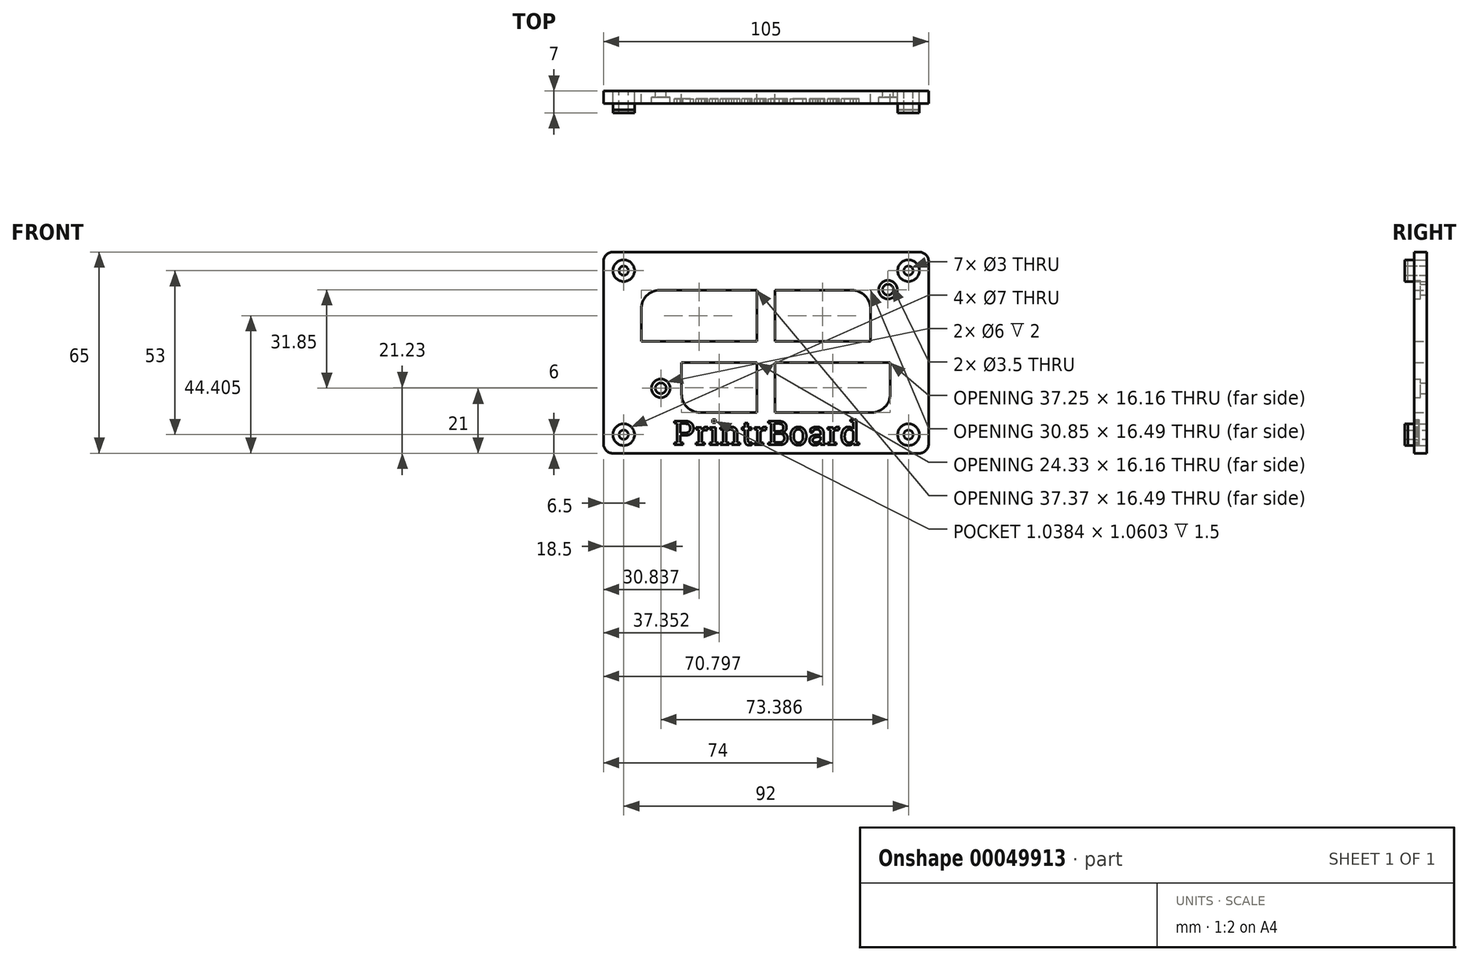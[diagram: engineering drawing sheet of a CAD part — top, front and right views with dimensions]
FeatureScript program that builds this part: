
annotation { "Feature Type Name" : "Feature", "Feature Type Description" : "" }
export const myFeature = defineFeature(function(context is Context, id is Id, definition is map)
    precondition{}
    {
        {
            var Q0;
            Q0=qCreatedBy(makeId("Front.planeOp"),FACE);
            var sketch = newSketch(context, id + "F0", { "sketchPlane" : qUnion([Q0])});
            skLineSegment(sketch, "E0.rect.bottom", {"start": v(46, -26.5) * mm, "end": v(-46, -26.5) * mm, "construction": true});
            skLineSegment(sketch, "E0.rect.top", {"start": v(46, 26.5) * mm, "end": v(-46, 26.5) * mm, "construction": true});
            skLineSegment(sketch, "E0.rect.left", {"start": v(46, -26.5) * mm, "end": v(46, 26.5) * mm, "construction": true});
            skLineSegment(sketch, "E0.rect.right", {"start": v(-46, -26.5) * mm, "end": v(-46, 26.5) * mm, "construction": true});
            skPoint(sketch, "E0.rect.middle", {"position": v(0, 0) * mm});
            skCircle(sketch, "E1", {"center": v(-46, 26.5) * mm, "radius": 3.5 * mm});
            skCircle(sketch, "E2", {"center": v(-46, -26.5) * mm, "radius": 3.5 * mm});
            skCircle(sketch, "E3", {"center": v(46, -26.5) * mm, "radius": 3.5 * mm});
            skCircle(sketch, "E4", {"center": v(46, 26.5) * mm, "radius": 3.5 * mm});
            skCircle(sketch, "E5", {"center": v(46, 26.5) * mm, "radius": 1.5 * mm});
            skCircle(sketch, "E6", {"center": v(46, -26.5) * mm, "radius": 1.5 * mm});
            skCircle(sketch, "E7", {"center": v(-46, -26.5) * mm, "radius": 1.5 * mm});
            skCircle(sketch, "E8", {"center": v(-46, 26.5) * mm, "radius": 1.5 * mm});
            skLineSegment(sketch, "E9.rect.bottom", {"start": v(49.5, -32.5) * mm, "end": v(-49.5, -32.5) * mm});
            skLineSegment(sketch, "E9.rect.top", {"start": v(49.5, 32.5) * mm, "end": v(-49.5, 32.5) * mm});
            skLineSegment(sketch, "E9.rect.left", {"start": v(52.5, -29.5) * mm, "end": v(52.5, 29.5) * mm});
            skLineSegment(sketch, "E9.rect.right", {"start": v(-52.5, -29.5) * mm, "end": v(-52.5, 29.5) * mm});
            skCircle(sketch, "E10", {"center": v(-34, -11.5) * mm, "radius": 3 * mm});
            skCircle(sketch, "E11", {"center": v(39.39, 20.35) * mm, "radius": 3 * mm});
            skCircle(sketch, "E12", {"center": v(-34, -11.5) * mm, "radius": 1.75 * mm});
            skCircle(sketch, "E13", {"center": v(39.39, 20.35) * mm, "radius": 1.75 * mm});
            skLineSegment(sketch, "E14.bottom", {"start": v(-34.35, 20.15) * mm, "end": v(-2.98, 20.15) * mm});
            skLineSegment(sketch, "E14.top", {"start": v(-40.35, 3.66) * mm, "end": v(-2.98, 3.66) * mm});
            skLineSegment(sketch, "E14.left", {"start": v(-40.35, 14.15) * mm, "end": v(-40.35, 3.66) * mm});
            skLineSegment(sketch, "E14.right", {"start": v(-2.98, 20.15) * mm, "end": v(-2.98, 3.66) * mm});
            skLineSegment(sketch, "E15.bottom", {"start": v(-2.98, -3.19) * mm, "end": v(-27.31, -3.19) * mm});
            skLineSegment(sketch, "E15.top", {"start": v(-2.98, -19.35) * mm, "end": v(-21.31, -19.35) * mm});
            skLineSegment(sketch, "E15.left", {"start": v(-2.98, -3.19) * mm, "end": v(-2.98, -19.35) * mm});
            skLineSegment(sketch, "E15.right", {"start": v(-27.31, -3.19) * mm, "end": v(-27.31, -13.35) * mm});
            skLineSegment(sketch, "E16.bottom", {"start": v(2.87, 3.66) * mm, "end": v(33.72, 3.66) * mm});
            skLineSegment(sketch, "E16.top", {"start": v(2.87, 20.15) * mm, "end": v(27.72, 20.15) * mm});
            skLineSegment(sketch, "E16.left", {"start": v(2.87, 3.66) * mm, "end": v(2.87, 20.15) * mm});
            skLineSegment(sketch, "E16.right", {"start": v(33.72, 3.66) * mm, "end": v(33.72, 14.15) * mm});
            skLineSegment(sketch, "E17.bottom", {"start": v(2.87, -3.19) * mm, "end": v(40.13, -3.19) * mm});
            skLineSegment(sketch, "E17.top", {"start": v(2.87, -19.35) * mm, "end": v(34.13, -19.35) * mm});
            skLineSegment(sketch, "E17.left", {"start": v(2.87, -3.19) * mm, "end": v(2.87, -19.35) * mm});
            skLineSegment(sketch, "E17.right", {"start": v(40.13, -3.19) * mm, "end": v(40.13, -13.35) * mm});
            skPoint(sketch, "E18.visualSharp", {"position": v(-40.35, 20.15) * mm});
            skArc(sketch, "E18.filletArc", {"start": v(-34.35, 20.15) * mm, "mid": v(-38.59, 18.4) * mm, "end": v(-40.35, 14.15) * mm});
            skPoint(sketch, "E19.visualSharp", {"position": v(-27.31, -19.35) * mm});
            skArc(sketch, "E19.filletArc", {"start": v(-27.31, -13.35) * mm, "mid": v(-25.56, -17.6) * mm, "end": v(-21.31, -19.35) * mm});
            skPoint(sketch, "E20.visualSharp", {"position": v(40.13, -19.35) * mm});
            skArc(sketch, "E20.filletArc", {"start": v(34.13, -19.35) * mm, "mid": v(38.37, -17.6) * mm, "end": v(40.13, -13.35) * mm});
            skPoint(sketch, "E21.visualSharp", {"position": v(33.72, 20.15) * mm});
            skArc(sketch, "E21.filletArc", {"start": v(33.72, 14.15) * mm, "mid": v(31.96, 18.4) * mm, "end": v(27.72, 20.15) * mm});
            skPoint(sketch, "E22.visualSharp", {"position": v(-52.5, 32.5) * mm});
            skArc(sketch, "E22.filletArc", {"start": v(-49.5, 32.5) * mm, "mid": v(-51.62, 31.62) * mm, "end": v(-52.5, 29.5) * mm});
            skPoint(sketch, "E23.visualSharp", {"position": v(-52.5, -32.5) * mm});
            skArc(sketch, "E23.filletArc", {"start": v(-52.5, -29.5) * mm, "mid": v(-51.62, -31.62) * mm, "end": v(-49.5, -32.5) * mm});
            skPoint(sketch, "E24.visualSharp", {"position": v(52.5, -32.5) * mm});
            skArc(sketch, "E24.filletArc", {"start": v(49.5, -32.5) * mm, "mid": v(51.62, -31.62) * mm, "end": v(52.5, -29.5) * mm});
            skPoint(sketch, "E25.visualSharp", {"position": v(52.5, 32.5) * mm});
            skArc(sketch, "E25.filletArc", {"start": v(52.5, 29.5) * mm, "mid": v(51.62, 31.62) * mm, "end": v(49.5, 32.5) * mm});
            skText(sketch, "E26", { "text": "PrintrBoard", "fontName": "RobotoSlab-Regular.ttf"});
            const initialGuessF0  = {"E26": [-0.02995, -0.0298, 1, 0, 0.00778]};
            skSetInitialGuess(sketch, initialGuessF0);
            skSolve(sketch);
        }
        {
            var Q0;
            Q0=makeQuery(id+"F0.imprint","IMPRINT",FACE,{"disambiguationData":[TD([[makeQuery(id+"F0.imprint","IMPRINT",EDGE,{"derivedFrom":sQuery(id+"F0.wireOp",EDGE,"E2")}),1.0]])]});
            var Q1;
            Q1=makeQuery(id+"F0.imprint","IMPRINT",FACE,{"disambiguationData":[TD([[makeQuery(id+"F0.imprint","IMPRINT",EDGE,{"derivedFrom":sQuery(id+"F0.wireOp",EDGE,"E1")}),1.0]])]});
            var Q2;
            Q2=makeQuery(id+"F0.imprint","IMPRINT",FACE,{"disambiguationData":[TD([[makeQuery(id+"F0.imprint","IMPRINT",EDGE,{"derivedFrom":sQuery(id+"F0.wireOp",EDGE,"E4")}),1.0]])]});
            var Q3;
            Q3=makeQuery(id+"F0.imprint","IMPRINT",FACE,{"disambiguationData":[TD([[makeQuery(id+"F0.imprint","IMPRINT",EDGE,{"derivedFrom":sQuery(id+"F0.wireOp",EDGE,"E3")}),1.0]])]});
            extrude(context, id + "F1", {"entities" : qUnion([Q0, Q1, Q2, Q3]), "depth" : 6 * mm});
        }
        {
            var Q0;
            Q0=makeQuery(id+"F0.imprint","IMPRINT",FACE,{"disambiguationData":[TD([[makeQuery(id+"F0.imprint","IMPRINT",EDGE,{"derivedFrom":sQuery(id+"F0.wireOp",EDGE,"E1")}),-1.0]])]});
            extrude(context, id + "F2", {"entities" : qUnion([Q0]), "depth" : 4 * mm});
        }
        {
            var Q0;
            Q0=makeQuery(id+"F0.imprint","IMPRINT",FACE,{"disambiguationData":[TD([[makeQuery(id+"F0.imprint","IMPRINT",EDGE,{"derivedFrom":sQuery(id+"F0.wireOp",EDGE,"E11")}),1.0]])]});
            var Q1;
            Q1=makeQuery(id+"F0.imprint","IMPRINT",FACE,{"disambiguationData":[TD([[makeQuery(id+"F0.imprint","IMPRINT",EDGE,{"derivedFrom":sQuery(id+"F0.wireOp",EDGE,"E10")}),1.0]])]});
            extrude(context, id + "F3", {"entities" : qUnion([Q0, Q1]), "operationType" : NewBodyOperationType.ADD, "depth" : 1 * mm});
        }
        {
            var Q0;
            Q0=makeQuery(id+"F1.opExtrude","CAP_FACE",FACE,{"disambiguationData":[OSD([sQuery(id+"F0.wireOp",EDGE,"E1"),sQuery(id+"F0.wireOp",EDGE,"E8")])],"isStart":false});
            var Q1;
            Q1=makeQuery(id+"F1.opExtrude","CAP_FACE",FACE,{"disambiguationData":[OSD([sQuery(id+"F0.wireOp",EDGE,"E2"),sQuery(id+"F0.wireOp",EDGE,"E7")])],"isStart":false});
            var Q2;
            Q2=makeQuery(id+"F1.opExtrude","CAP_FACE",FACE,{"disambiguationData":[OSD([sQuery(id+"F0.wireOp",EDGE,"E3"),sQuery(id+"F0.wireOp",EDGE,"E6")])],"isStart":false});
            extrude(context, id + "F4", {"entities" : qUnion([Q0, Q1, Q2]), "depth" : 1 * mm});
        }
        {
            var Q0;
            Q0=makeQuery(id+"F1.opExtrude","CAP_FACE",FACE,{"disambiguationData":[OSD([sQuery(id+"F0.wireOp",EDGE,"E4"),sQuery(id+"F0.wireOp",EDGE,"E5")])],"isStart":false});
            extrude(context, id + "F5", {"entities" : qUnion([Q0]), "operationType" : NewBodyOperationType.ADD, "depth" : 1 * mm});
        }
        {
            var Q0;
            Q0=makeQuery(id+"F3.opExtrude","CAP_FACE",FACE,{"disambiguationData":[OSD([sQuery(id+"F0.wireOp",EDGE,"E11"),sQuery(id+"F0.wireOp",EDGE,"E13")])],"isStart":false});
            var Q1;
            Q1=makeQuery(id+"F3.opExtrude","CAP_FACE",FACE,{"disambiguationData":[OSD([sQuery(id+"F0.wireOp",EDGE,"E10"),sQuery(id+"F0.wireOp",EDGE,"E12")])],"isStart":false});
            extrude(context, id + "F6", {"entities" : qUnion([Q0, Q1]), "operationType" : NewBodyOperationType.ADD, "depth" : 1 * mm});
        }
        {
            var Q0;
            Q0=makeQuery(id+"F0.imprint","IMPRINT",FACE,{"disambiguationData":[TD([[makeQuery(id+"F0.imprint","IMPRINT",EDGE,{"derivedFrom":sQuery(id+"F0.wireOp",EDGE,"E26.sketch_text.stroke-0")}),-1.0]])]});
            var Q1;
            Q1=makeQuery(id+"F0.imprint","IMPRINT",FACE,{"disambiguationData":[TD([[makeQuery(id+"F0.imprint","IMPRINT",EDGE,{"derivedFrom":sQuery(id+"F0.wireOp",EDGE,"E26.sketch_text.stroke-23")}),-1.0]])]});
            var Q2;
            Q2=makeQuery(id+"F0.imprint","IMPRINT",FACE,{"disambiguationData":[TD([[makeQuery(id+"F0.imprint","IMPRINT",EDGE,{"derivedFrom":sQuery(id+"F0.wireOp",EDGE,"E26.sketch_text.stroke-42")}),-1.0]])]});
            var Q3;
            Q3=makeQuery(id+"F0.imprint","IMPRINT",FACE,{"disambiguationData":[TD([[makeQuery(id+"F0.imprint","IMPRINT",EDGE,{"derivedFrom":sQuery(id+"F0.wireOp",EDGE,"E26.sketch_text.stroke-52")}),-1.0]])]});
            var Q4;
            Q4=makeQuery(id+"F0.imprint","IMPRINT",FACE,{"disambiguationData":[TD([[makeQuery(id+"F0.imprint","IMPRINT",EDGE,{"derivedFrom":sQuery(id+"F0.wireOp",EDGE,"E26.sketch_text.stroke-56")}),-1.0]])]});
            var Q5;
            Q5=makeQuery(id+"F0.imprint","IMPRINT",FACE,{"disambiguationData":[TD([[makeQuery(id+"F0.imprint","IMPRINT",EDGE,{"derivedFrom":sQuery(id+"F0.wireOp",EDGE,"E26.sketch_text.stroke-82")}),-1.0]])]});
            var Q6;
            Q6=makeQuery(id+"F0.imprint","IMPRINT",FACE,{"disambiguationData":[TD([[makeQuery(id+"F0.imprint","IMPRINT",EDGE,{"derivedFrom":sQuery(id+"F0.wireOp",EDGE,"E26.sketch_text.stroke-102")}),-1.0]])]});
            var Q7;
            Q7=makeQuery(id+"F0.imprint","IMPRINT",FACE,{"disambiguationData":[TD([[makeQuery(id+"F0.imprint","IMPRINT",EDGE,{"derivedFrom":sQuery(id+"F0.wireOp",EDGE,"E26.sketch_text.stroke-121")}),-1.0]])]});
            var Q8;
            Q8=makeQuery(id+"F0.imprint","IMPRINT",FACE,{"disambiguationData":[TD([[makeQuery(id+"F0.imprint","IMPRINT",EDGE,{"derivedFrom":sQuery(id+"F0.wireOp",EDGE,"E26.sketch_text.stroke-151")}),-1.0]])]});
            var Q9;
            Q9=makeQuery(id+"F0.imprint","IMPRINT",FACE,{"disambiguationData":[TD([[makeQuery(id+"F0.imprint","IMPRINT",EDGE,{"derivedFrom":sQuery(id+"F0.wireOp",EDGE,"E26.sketch_text.stroke-171")}),-1.0]])]});
            var Q10;
            Q10=makeQuery(id+"F0.imprint","IMPRINT",FACE,{"disambiguationData":[TD([[makeQuery(id+"F0.imprint","IMPRINT",EDGE,{"derivedFrom":sQuery(id+"F0.wireOp",EDGE,"E26.sketch_text.stroke-206")}),-1.0]])]});
            var Q11;
            Q11=makeQuery(id+"F0.imprint","IMPRINT",FACE,{"disambiguationData":[TD([[makeQuery(id+"F0.imprint","IMPRINT",EDGE,{"derivedFrom":sQuery(id+"F0.wireOp",EDGE,"E26.sketch_text.stroke-225")}),-1.0]])]});
            extrude(context, id + "F7", {"entities" : qUnion([Q0, Q1, Q2, Q3, Q4, Q5, Q6, Q7, Q8, Q9, Q10, Q11]), "operationType" : NewBodyOperationType.ADD, "depth" : 2.5 * mm});
        }
        {
            var Q0;
            Q0=makeQuery(id+"F0.imprint","IMPRINT",FACE,{"disambiguationData":[TD([[makeQuery(id+"F0.imprint","IMPRINT",EDGE,{"derivedFrom":sQuery(id+"F0.wireOp",EDGE,"E26.sketch_text.stroke-16")}),1.0]])]});
            var Q1;
            Q1=makeQuery(id+"F0.imprint","IMPRINT",FACE,{"disambiguationData":[TD([[makeQuery(id+"F0.imprint","IMPRINT",EDGE,{"derivedFrom":sQuery(id+"F0.wireOp",EDGE,"E26.sketch_text.stroke-144")}),1.0]])]});
            var Q2;
            Q2=makeQuery(id+"F0.imprint","IMPRINT",FACE,{"disambiguationData":[TD([[makeQuery(id+"F0.imprint","IMPRINT",EDGE,{"derivedFrom":sQuery(id+"F0.wireOp",EDGE,"E26.sketch_text.stroke-137")}),1.0]])]});
            var Q3;
            Q3=makeQuery(id+"F0.imprint","IMPRINT",FACE,{"disambiguationData":[TD([[makeQuery(id+"F0.imprint","IMPRINT",EDGE,{"derivedFrom":sQuery(id+"F0.wireOp",EDGE,"E26.sketch_text.stroke-161")}),1.0]])]});
            var Q4;
            Q4=makeQuery(id+"F0.imprint","IMPRINT",FACE,{"disambiguationData":[TD([[makeQuery(id+"F0.imprint","IMPRINT",EDGE,{"derivedFrom":sQuery(id+"F0.wireOp",EDGE,"E26.sketch_text.stroke-198")}),1.0]])]});
            var Q5;
            Q5=makeQuery(id+"F0.imprint","IMPRINT",FACE,{"disambiguationData":[TD([[makeQuery(id+"F0.imprint","IMPRINT",EDGE,{"derivedFrom":sQuery(id+"F0.wireOp",EDGE,"E26.sketch_text.stroke-244")}),1.0]])]});
            extrude(context, id + "F8", {"entities" : qUnion([Q0, Q1, Q2, Q3, Q4, Q5]), "operationType" : NewBodyOperationType.ADD, "depth" : 4 * mm});
        }
    });
